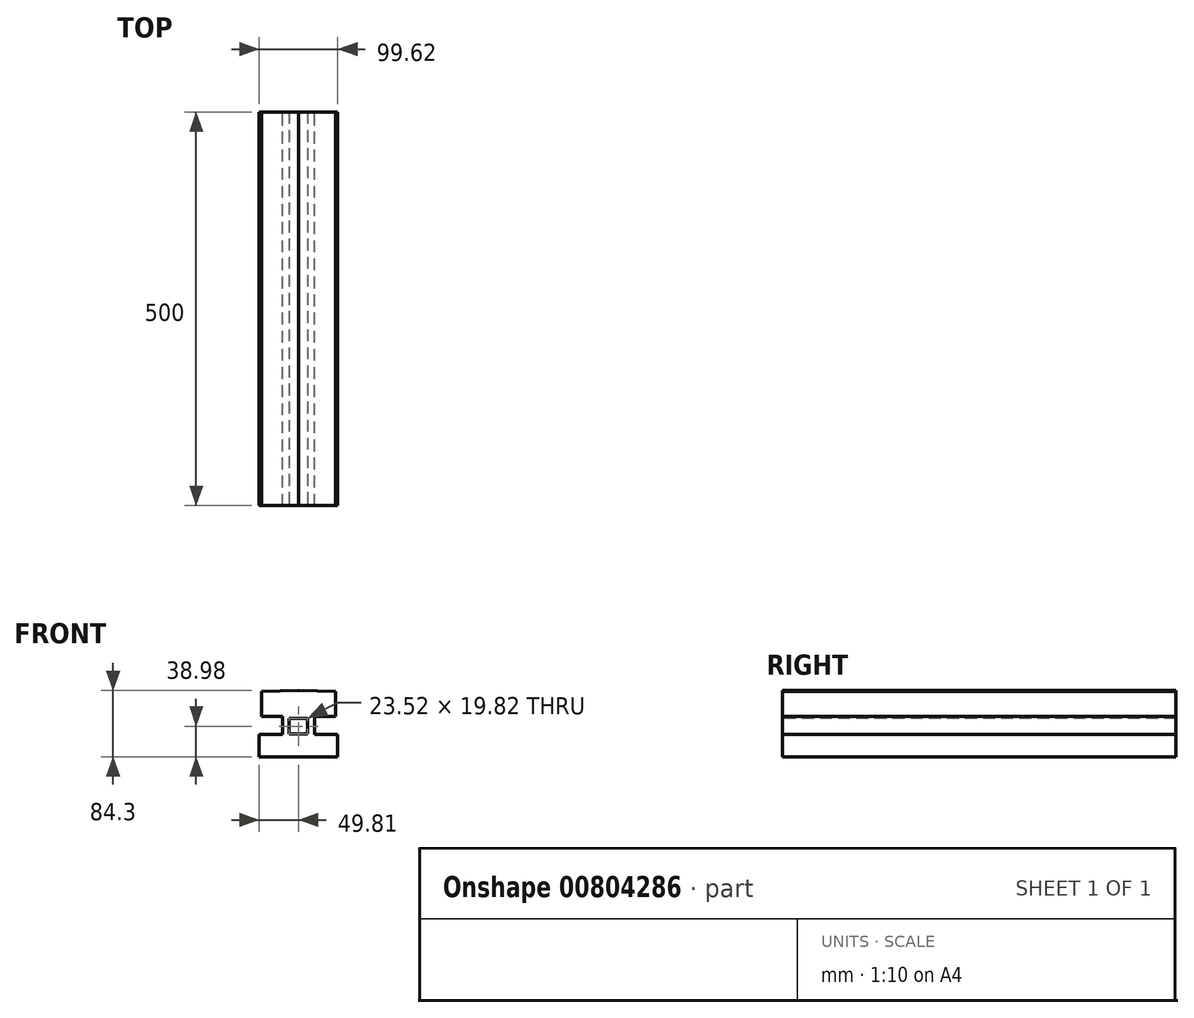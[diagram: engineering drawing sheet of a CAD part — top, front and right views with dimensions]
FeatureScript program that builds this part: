
annotation { "Feature Type Name" : "Feature", "Feature Type Description" : "" }
export const myFeature = defineFeature(function(context is Context, id is Id, definition is map)
    precondition{}
    {
        {
            var Q0;
            Q0=qCreatedBy(makeId("Front.planeOp"),FACE);
            var sketch = newSketch(context, id + "F0", { "sketchPlane" : qUnion([Q0])});
            skLineSegment(sketch, "E0", {"start": v(0, 45.32) * mm, "end": v(0, -38.98) * mm, "construction": true});
            skLineSegment(sketch, "E1", {"start": v(0, -38.98) * mm, "end": v(49.81, -38.98) * mm});
            skLineSegment(sketch, "E2", {"start": v(49.81, -38.98) * mm, "end": v(49.81, -10.17) * mm});
            skLineSegment(sketch, "E3", {"start": v(49.81, -10.17) * mm, "end": v(20.48, -10.17) * mm});
            skLineSegment(sketch, "E4", {"start": v(20.48, -10.17) * mm, "end": v(20.48, 12.82) * mm});
            skLineSegment(sketch, "E5", {"start": v(20.48, 12.82) * mm, "end": v(46.9, 12.82) * mm});
            skLineSegment(sketch, "E6", {"start": v(46.9, 12.82) * mm, "end": v(46.9, 44.26) * mm});
            skLineSegment(sketch, "E7", {"start": v(46.9, 44.26) * mm, "end": v(0, 45.32) * mm});
            skLineSegment(sketch, "E8.MirrorCS", {"start": v(-46.9, 44.26) * mm, "end": v(0, 45.32) * mm});
            skLineSegment(sketch, "E9.MirrorCS", {"start": v(-46.9, 12.82) * mm, "end": v(-46.9, 44.26) * mm});
            skLineSegment(sketch, "E10.MirrorCS", {"start": v(-20.48, 12.82) * mm, "end": v(-46.9, 12.82) * mm});
            skLineSegment(sketch, "E11.MirrorCS", {"start": v(-20.48, -10.17) * mm, "end": v(-20.48, 12.82) * mm});
            skLineSegment(sketch, "E12.MirrorCS", {"start": v(-49.81, -10.17) * mm, "end": v(-20.48, -10.17) * mm});
            skLineSegment(sketch, "E13.MirrorCS", {"start": v(-49.81, -38.98) * mm, "end": v(-49.81, -10.17) * mm});
            skLineSegment(sketch, "E14.MirrorCS", {"start": v(0, -38.98) * mm, "end": v(-49.81, -38.98) * mm});
            skSolve(sketch);
        }
        {
            var Q0;
            Q0 = qSketchRegion(id + "F0", true);
            extrude(context, id + "F1", {"entities" : qUnion([Q0]), "depth" : 500 * mm, "offsetDistance" : 25 * mm});
        }
        {
            var Q0;
            Q0=makeQuery(id+"F1.opExtrude","CAP_FACE",FACE,{"disambiguationData":[OSD([sQuery(id+"F0.wireOp",EDGE,"E1"),sQuery(id+"F0.wireOp",EDGE,"E2"),sQuery(id+"F0.wireOp",EDGE,"E3"),sQuery(id+"F0.wireOp",EDGE,"E4"),sQuery(id+"F0.wireOp",EDGE,"E5"),sQuery(id+"F0.wireOp",EDGE,"E6"),sQuery(id+"F0.wireOp",EDGE,"E7"),sQuery(id+"F0.wireOp",EDGE,"E8.MirrorCS"),sQuery(id+"F0.wireOp",EDGE,"E9.MirrorCS"),sQuery(id+"F0.wireOp",EDGE,"E10.MirrorCS"),sQuery(id+"F0.wireOp",EDGE,"E11.MirrorCS"),sQuery(id+"F0.wireOp",EDGE,"E12.MirrorCS"),sQuery(id+"F0.wireOp",EDGE,"E13.MirrorCS"),sQuery(id+"F0.wireOp",EDGE,"E14.MirrorCS")])],"isStart":false});
            var sketch = newSketch(context, id + "F2", { "sketchPlane" : qUnion([Q0])});
            skLineSegment(sketch, "E15.bottom", {"start": v(-11.76, 9.9) * mm, "end": v(11.76, 9.9) * mm});
            skLineSegment(sketch, "E15.top", {"start": v(-11.76, -9.9) * mm, "end": v(11.76, -9.9) * mm});
            skLineSegment(sketch, "E15.left", {"start": v(-11.76, 9.9) * mm, "end": v(-11.76, -9.9) * mm});
            skLineSegment(sketch, "E15.right", {"start": v(11.76, 9.9) * mm, "end": v(11.76, -9.9) * mm});
            skPoint(sketch, "E15.middle", {"position": v(0, 0) * mm});
            skSolve(sketch);
        }
        {
            var Q0;
            Q0 = qSketchRegion(id + "F2", true);
            extrude(context, id + "F3", {"entities" : qUnion([Q0]), "operationType" : NewBodyOperationType.REMOVE, "oppositeDirection" : true, "depth" : 500 * mm, "offsetDistance" : 25 * mm});
        }
    });
